# Revit family: PRD_FrankeWS_MxrTps_HygieneUnit_ACST9001
name_source: partatom
category: Specialty Equipment
revit_build: Autodesk Revit 2018 (Build: 20190510_1515(x64)
units: mm (PartAtom-declared; Revit-internal decimal feet)

## family parameters
Always vertical = No
Cut with Voids When Loaded = No
OmniClass Number = 23.45.05.14.99
OmniClass Title = Other Sanitary Washing Plumbing Fixtures
Part Type = Normal
Room Calculation Point = No
Round Connector Dimension = Use Diameter
Shared = No
Work Plane-Based = Yes

## types (1)
- ACST9001
    AssetType = Fixed
    BIMObjectName = PRD_AR_MixerTaps_HygieneUnit_ACST9001
    BodyMaterial = PRD_AR_ChromatedBrass_HighPolished
    Category = Pr_40_20_87_55, Mixer taps
    Color = Chrome
    Default Elevation = 1219 mm
    Description = Hygiene unit for F5S-Therm self-closing thermostatic wall mixers for sanitary and shower facilities, for performing of an automatic hygiene flushing and storage of statistical data. Housing adapter including sensor with control electronics and 6 V lithium battery (CR-P2) as well as solenoid valve cartridge. Activated water hygiene flushing (30 s), fixed interval time 24 hours and saving of statistical data. With option for parameterization and communication via optional, bidirectional remote control.
    DurationUnit = year
    Features = for performing of an automatic hygiene flushing, fixed interval time 24 hours
    Finish = Polished chrome
    GrossWeight = 0.76 kg
    IfcExportAs = IfcControllerType
    IfcExportType = USERDEFINED
    Manufacturer = KWC Group AG
    ManufacturerName = KWC Group AG
    ManufacturerURL = www.kwc.com
    Model = ACST9001
    ModelNumber = 2030041162
    ModelReference = ACST9001
    Name = Hygiene unit for F5S-Therm ACST9001
    NetWeight = 0.60 kg
    NominalDepth = 0 mm  [stored 0 ft]
    NominalHeight = 0 mm  [stored 0 ft]
    NominalWidth = 0 mm  [stored 0 ft]
    NumberOfBatteries = 1
    ProductCode = 210.0636.672
    ProductInformation = https://pim.kwc.com
    Quantity = 1
    QuantityUom = Piece
    SensorMaterial = PRD_Ar_Black
    Status = New
    TypeOfBatteries = CR-P2
    URL = www.kwc.com
    Uniclass2015Code = Pr_40_20_87_55
    Uniclass2015Title = Mixer taps
    Uniclass2015Version = Products v1.17
    Version = 1
    WarrantyDurationUnit = year

note: [stored X ft] marks values corroborated as IEEE doubles in the binary element streams (Revit-internal decimal feet)

## geometry (parser evidence)
native form markers: Sweep x3
no freeform markers — native parametric forms only
